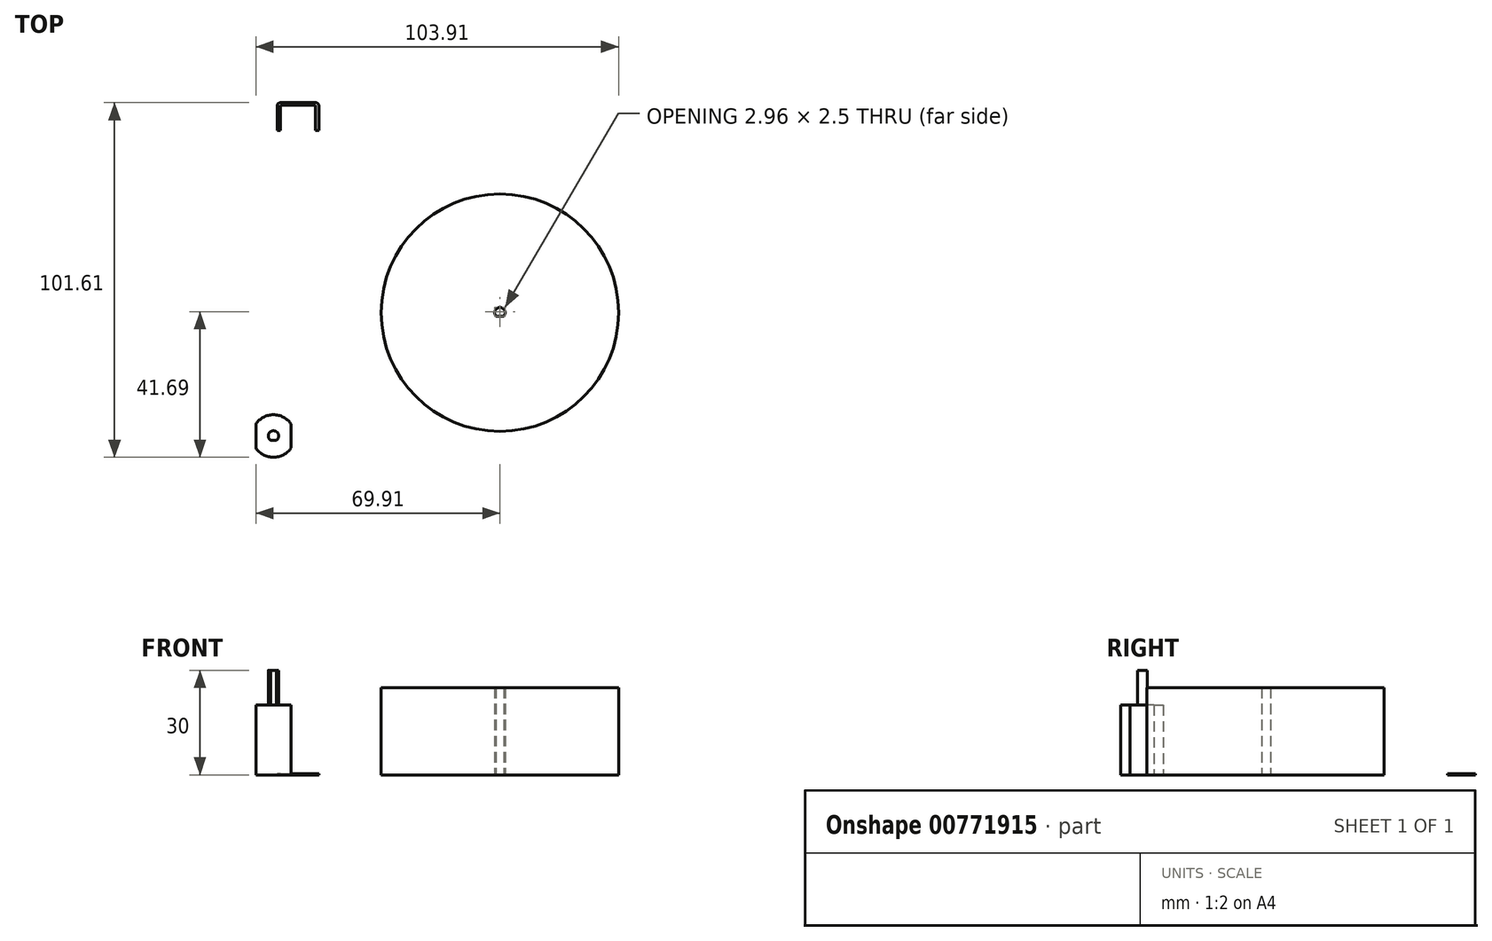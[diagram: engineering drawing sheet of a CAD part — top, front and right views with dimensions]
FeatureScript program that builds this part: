
annotation { "Feature Type Name" : "Feature", "Feature Type Description" : "" }
export const myFeature = defineFeature(function(context is Context, id is Id, definition is map)
    precondition{}
    {
        {
            var Q0;
            Q0=qCreatedBy(makeId("Top.planeOp"),FACE);
            var sketch = newSketch(context, id + "F0", { "sketchPlane" : qUnion([Q0])});
            skCircle(sketch, "E0", {"center": v(0, 0) * mm, "radius": 34 * mm});
            skCircle(sketch, "E1", {"center": v(0, 0) * mm, "radius": 1.5 * mm});
            skLineSegment(sketch, "E2", {"start": v(0, 1.5) * mm, "end": v(0, -1) * mm});
            skLineSegment(sketch, "E3", {"start": v(-1.12, -1) * mm, "end": v(1.12, -1) * mm});
            skSolve(sketch);
        }
        {
            var Q0;
            Q0 = qSketchRegion(id + "F0", true);
            var Q1;
            {var subQ0=sQuery(id+"F0.wireOp",EDGE,"E3");var subQ1=sQuery(id+"F0.wireOp",EDGE,"E1");var subQ2=makeQuery(id+"F0.imprint","INTERSECT",VERTEX,{"disambiguationData":[OD(0.0)],"derivedFrom":[subQ1,subQ0]});Q1=makeQuery(id+"F0.imprint","IMPRINT",FACE,{"disambiguationData":[TD([[makeQuery(id+"F0.imprint","IMPRINT",EDGE,{"disambiguationData":[TD([[subQ2,-1.0]])],"derivedFrom":subQ1}),1.0]])]});}
            extrude(context, id + "F1", {"entities" : qUnion([Q0, Q1]), "depth" : 25 * mm, "offsetDistance" : 25 * mm});
        }
        {
            var Q0;
            Q0=qCreatedBy(makeId("Top.planeOp"),FACE);
            var sketch = newSketch(context, id + "F2", { "sketchPlane" : qUnion([Q0])});
            skCircle(sketch, "E4", {"center": v(-64.85, -35.34) * mm, "radius": 6.1 * mm});
            skLineSegment(sketch, "E5.bottom", {"start": v(-69.91, -31.92) * mm, "end": v(-59.8, -31.92) * mm});
            skLineSegment(sketch, "E5.top", {"start": v(-69.91, -38.75) * mm, "end": v(-59.8, -38.75) * mm});
            skLineSegment(sketch, "E5.left", {"start": v(-69.91, -31.92) * mm, "end": v(-69.91, -38.75) * mm});
            skLineSegment(sketch, "E5.right", {"start": v(-59.8, -31.92) * mm, "end": v(-59.8, -38.75) * mm});
            skSolve(sketch);
        }
        {
            var Q0;
            {var subQ0=sQuery(id+"F2.wireOp",EDGE,"E5.left");var subQ1=sQuery(id+"F2.wireOp",EDGE,"E4");var subQ2=makeQuery(id+"F2.imprint","INTERSECT",VERTEX,{"derivedFrom":[subQ1,subQ0]});Q0=makeQuery(id+"F2.imprint","IMPRINT",FACE,{"disambiguationData":[TD([[makeQuery(id+"F2.imprint","IMPRINT",EDGE,{"disambiguationData":[TD([[subQ2,-1.0]])],"derivedFrom":subQ1}),-1.0]])]});}
            var Q1;
            {var subQ0=sQuery(id+"F2.wireOp",EDGE,"E5.top");Q1=makeQuery(id+"F2.imprint","IMPRINT",FACE,{"disambiguationData":[TD([[makeQuery(id+"F2.imprint","IMPRINT",EDGE,{"derivedFrom":subQ0}),-1.0]])]});}
            var Q2;
            {var subQ0=sQuery(id+"F2.wireOp",EDGE,"E5.bottom");Q2=makeQuery(id+"F2.imprint","IMPRINT",FACE,{"disambiguationData":[TD([[makeQuery(id+"F2.imprint","IMPRINT",EDGE,{"derivedFrom":subQ0}),1.0]])]});}
            var Q3;
            Q3=makeQuery(id+"F2.imprint","IMPRINT",FACE,{"disambiguationData":[TD([[makeQuery(id+"F2.imprint","IMPRINT",EDGE,{"derivedFrom":sQuery(id+"F2.wireOp",EDGE,"E5.bottom")}),-1.0]])]});
            extrude(context, id + "F3", {"entities" : qUnion([Q0, Q1, Q2, Q3]), "depth" : 20 * mm, "offsetDistance" : 25 * mm});
        }
        {
            var Q0;
            Q0=makeQuery(id+"F3.opExtrude","CAP_FACE",FACE,{"disambiguationData":[OSD([sQuery(id+"F2.wireOp",EDGE,"E4"),sQuery(id+"F2.wireOp",EDGE,"E5.left"),sQuery(id+"F2.wireOp",EDGE,"E5.right")])],"isStart":false});
            var sketch = newSketch(context, id + "F4", { "sketchPlane" : qUnion([Q0])});
            skCircle(sketch, "E6", {"center": v(-64.85, -35.34) * mm, "radius": 1.5 * mm});
            skLineSegment(sketch, "E7", {"start": v(-64.85, -35.34) * mm, "end": v(-64.85, -36.59) * mm});
            skLineSegment(sketch, "E8", {"start": v(-64.85, -36.59) * mm, "end": v(-64.02, -36.59) * mm});
            skLineSegment(sketch, "E9", {"start": v(-64.02, -36.59) * mm, "end": v(-65.6, -36.59) * mm});
            skLineSegment(sketch, "E10", {"start": v(-65.6, -36.59) * mm, "end": v(-65.68, -36.59) * mm});
            skSolve(sketch);
        }
        {
            var Q0;
            {var subQ3=sQuery(id+"F4.wireOp",EDGE,"E10");Q0=makeQuery(id+"F4.imprint","IMPRINT",FACE,{"disambiguationData":[TD([[makeQuery(id+"F4.imprint","IMPRINT",EDGE,{"derivedFrom":subQ3}),-1.0]])]});}
            extrude(context, id + "F5", {"entities" : qUnion([Q0]), "operationType" : NewBodyOperationType.ADD, "depth" : 10 * mm, "offsetDistance" : 25 * mm});
        }
        {
            var Q0;
            Q0=qCreatedBy(makeId("Top.planeOp"),FACE);
            var sketch = newSketch(context, id + "F6", { "sketchPlane" : qUnion([Q0])});
            skLineSegment(sketch, "E11.bottom", {"start": v(-63.82, 60.17) * mm, "end": v(-51.82, 60.17) * mm});
            skLineSegment(sketch, "E11.top", {"start": v(-63.82, 52.17) * mm, "end": v(-51.82, 52.17) * mm});
            skLineSegment(sketch, "E11.left", {"start": v(-63.82, 59.17) * mm, "end": v(-63.82, 52.17) * mm});
            skLineSegment(sketch, "E11.right", {"start": v(-51.82, 59.17) * mm, "end": v(-51.82, 52.17) * mm});
            skLineSegment(sketch, "E12", {"start": v(-62.82, 60.17) * mm, "end": v(-62.82, 60.17) * mm});
            skLineSegment(sketch, "E13", {"start": v(-52.82, 60.17) * mm, "end": v(-52.82, 60.17) * mm});
            skLineSegment(sketch, "E14", {"start": v(-62.82, 60.17) * mm, "end": v(-62.82, 59.47) * mm});
            skLineSegment(sketch, "E15", {"start": v(-62.82, 59.47) * mm, "end": v(-52.82, 59.47) * mm});
            skLineSegment(sketch, "E16", {"start": v(-52.82, 59.47) * mm, "end": v(-52.82, 60.17) * mm});
            skLineSegment(sketch, "E17.top", {"start": v(-62.82, 52.17) * mm, "end": v(-52.82, 52.17) * mm});
            skLineSegment(sketch, "E17.left", {"start": v(-62.82, 59.47) * mm, "end": v(-62.82, 52.17) * mm});
            skLineSegment(sketch, "E17.right", {"start": v(-52.82, 59.47) * mm, "end": v(-52.82, 52.17) * mm});
            skPoint(sketch, "E18.visualSharp", {"position": v(-51.82, 60.17) * mm});
            skArc(sketch, "E18.filletArc", {"start": v(-51.82, 59.17) * mm, "mid": v(-52.1, 59.88) * mm, "end": v(-52.82, 60.17) * mm});
            skPoint(sketch, "E19.visualSharp", {"position": v(-63.82, 60.17) * mm});
            skArc(sketch, "E19.filletArc", {"start": v(-62.82, 60.17) * mm, "mid": v(-63.52, 59.88) * mm, "end": v(-63.82, 59.17) * mm});
            skSolve(sketch);
        }
        {
            var Q0;
            {var subQ1=sQuery(id+"F6.wireOp",EDGE,"E11.left");Q0=makeQuery(id+"F6.imprint","IMPRINT",FACE,{"disambiguationData":[TD([[makeQuery(id+"F6.imprint","IMPRINT",EDGE,{"derivedFrom":subQ1}),1.0]])]});}
            var Q1;
            {var subQ1=sQuery(id+"F6.wireOp",EDGE,"E11.right");Q1=makeQuery(id+"F6.imprint","IMPRINT",FACE,{"disambiguationData":[TD([[makeQuery(id+"F6.imprint","IMPRINT",EDGE,{"derivedFrom":subQ1}),-1.0]])]});}
            var Q2;
            {var subQ0=sQuery(id+"F6.wireOp",EDGE,"E14");Q2=makeQuery(id+"F6.imprint","IMPRINT",FACE,{"disambiguationData":[TD([[makeQuery(id+"F6.imprint","IMPRINT",EDGE,{"derivedFrom":subQ0}),1.0]])]});}
            extrude(context, id + "F7", {"entities" : qUnion([Q0, Q1, Q2]), "depth" : 0.3 * mm, "offsetDistance" : 25 * mm});
        }
        {
            var Q0;
            {var subQ0=sQuery(id+"F6.wireOp",EDGE,"E11.top");Q0=makeQuery(id+"F7.opExtrude","SWEPT_FACE",FACE,{"disambiguationData":[OSD([subQ0]),TDD([makeQuery(id+"F6.imprint","IMPRINT",EDGE,{"disambiguationData":[TD([[makeQuery(id+"F6.imprint","INTERSECT",VERTEX,{"derivedFrom":[subQ0,sQuery(id+"F6.wireOp",EDGE,"E17.left")]}),1.0]])],"derivedFrom":subQ0})])]});}
            var sketch = newSketch(context, id + "F8", { "sketchPlane" : qUnion([Q0])});
            skLineSegment(sketch, "E20", {"start": v(-63.32, 0.3) * mm, "end": v(-63.32, 0) * mm});
            skCircle(sketch, "E21", {"center": v(-63.32, 0.15) * mm, "radius": 0.15 * mm});
            skSolve(sketch);
        }
        {
            var Q0;
            Q0 = qSketchRegion(id + "F8", true);
            extrude(context, id + "F9", {"entities" : qUnion([Q0]), "operationType" : NewBodyOperationType.REMOVE, "oppositeDirection" : true, "depth" : -8 * mm, "offsetDistance" : 25 * mm});
        }
    });
